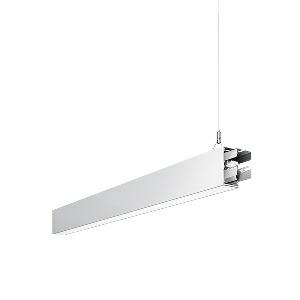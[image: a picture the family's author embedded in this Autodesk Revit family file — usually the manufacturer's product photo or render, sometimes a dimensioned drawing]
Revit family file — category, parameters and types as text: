
# Revit family: dotoo_line_-_dlp_2000_840_d_mid_00805782_54a0
name_source: partatom
category: Lighting Fixtures
units: mm (PartAtom-declared; Revit-internal decimal feet)

## family parameters
Cut with Voids When Loaded = No
Host = Face
Light Source = No
Part Type = Normal
Room Calculation Point = No
Round Connector Dimension = Use Diameter
Shared = No

## types (1)
- DOTOO.line - DLP 2000/840/D MID (1 x LED, 1700 lm, 4000K)
    Apparent Load = 16 VA
    Approval mark = CE
    CIE Flux Codes = 67 91 98 100 100
    Color Rendering = 80-89
    Color Temperature = 4000K
    Control Gear = Electronic ballast
    Default Elevation = 1800 mm
    Description = DLP 2000/840/D|Suspended luminaire|light source: LED|connected load: 220-240 V, 50/60 Hz|Power consumption: approx. 16 W|standby: approx. 0,15|luminous flux: 1700 lm|luminous efficacy: 106 lm/W|light distribution: Direct|direct ratio: approx. 100 %|colour temperature: Cold white, ca. 4000 K|color rendering index (CRI): >= 80|chromaticity tolerance:  3 SDCM|System of protection: IP 40|technology: Continuously dimmable|luminaire body|material: Sectional aluminium|colour: White|lamp cover: Acrylic (PMMA), Clear|mains lead: 1,0 m With free stranded wires|Fastening: Steel cable 0.3 - 0.7 m|glare control: Prism aperture|luminance(L65): <= 3000 cd/m|unified glare rating(4H 8H): <=  19|special features: DALI Load 1x, TouchDIM - dimming via standard switch, Through-wired, up to 18 m on one mains connection, Flicker-free, Suitable as emergency lighting, Mechanical and electrical connection of the individual modules without tools|
    Frequency = 50 Hz
    Height = 110 mm
    Lamp = 1 x LED
    Lamp Light Flux = 1700 lm
    Lamp count = 1
    Length = 1402 mm
    Luminous efficacy = 106 lm/W
    Manufacturer = Waldmann
    ModVariant = No
    Model = 00805782
    Mounting Place = Ceiling
    Mounting Type = Pendant
    Number of Poles = 1
    OnlyDefault = Yes
    Power Factor = 1
    Product Name = DOTOO.line - DLP 2000/840/D MID
    Product group = Suspended luminaire
    ProductGroupID = 9
    Protection Class = Protection class I
    Protection Degree = IP 40
    RLX_Detail_Level = 1
    RLX_Emergency_Light_Flux = 0 lm
    RLX_Emergency_Type = 0
    RLX_Emergency_Type_DB = No
    RlxData = <blob elided: 20545 chars, md5=8e9adfaa>
    Socket = socket
    Standby Power = 0 W
    System Light Flux = 1700 lm
    System Power = 16 W
    Type Comments = Product without accessories
    Type Image = 113308000-00692588.jpg
    URL = http://relux.com
    VarID = ---
    Voltage = 230 V
    Voltage Range = 220-240 V
    Weight = 0.00 kg
    Width = 60 mm  [stored 0.19685 ft]

note: [stored X ft] marks values corroborated as IEEE doubles in the binary element streams (Revit-internal decimal feet)

## geometry (parser evidence)
native form markers: Blend x4, Sweep x11
no freeform markers — native parametric forms only
